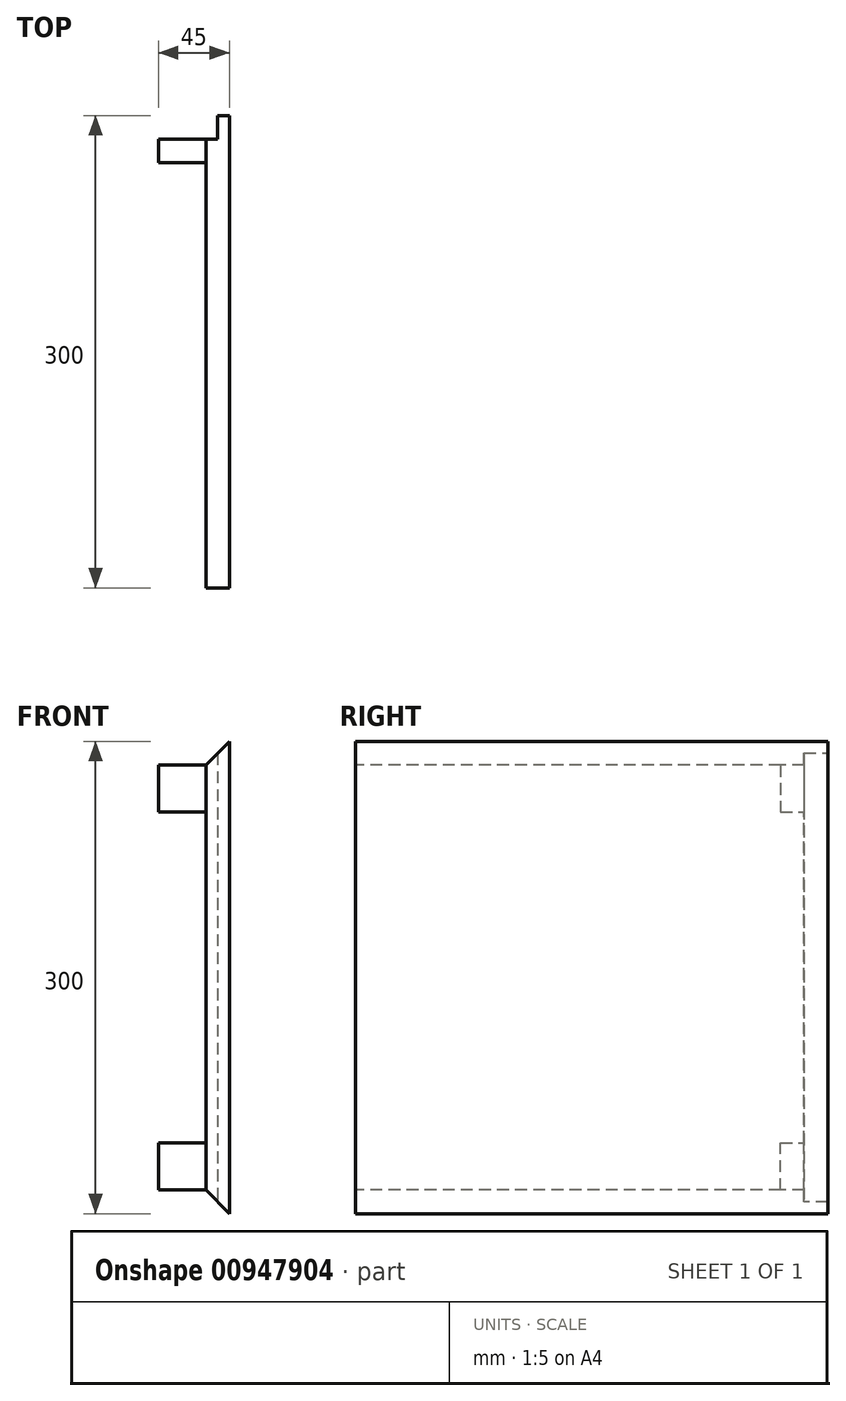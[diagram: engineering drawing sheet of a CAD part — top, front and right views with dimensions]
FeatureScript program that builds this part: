
annotation { "Feature Type Name" : "Feature", "Feature Type Description" : "" }
export const myFeature = defineFeature(function(context is Context, id is Id, definition is map)
    precondition{}
    {
        {
            var Q0;
            Q0=qCreatedBy(makeId("Right.planeOp"),FACE);
            cPlane(context, id + "F0", {"entities" : qUnion([Q0]), "cplaneType" : CPlaneType.OFFSET, "offset" : 100 * mm, "width" : 150 * mm, "height" : 150 * mm});
        }
        {
            var Q0;
            Q0=qCreatedBy(makeId("Front.planeOp"),FACE);
            cPlane(context, id + "F1", {"entities" : qUnion([Q0]), "cplaneType" : CPlaneType.OFFSET, "offset" : 150 * mm, "width" : 150 * mm, "height" : 150 * mm});
        }
        {
            var Q0;
            Q0=qCreatedBy(makeId("Front.planeOp"),FACE);
            cPlane(context, id + "F2", {"entities" : qUnion([Q0]), "cplaneType" : CPlaneType.OFFSET, "offset" : 150 * mm, "oppositeDirection" : true, "width" : 150 * mm, "height" : 150 * mm});
        }
        {
            var Q0;
            Q0=qCreatedBy(makeId("Top.planeOp"),FACE);
            cPlane(context, id + "F3", {"entities" : qUnion([Q0]), "cplaneType" : CPlaneType.OFFSET, "offset" : 300 * mm, "width" : 150 * mm, "height" : 150 * mm});
        }
        {
            var Q0;
            Q0=qCreatedBy(id+"F1.planeOp",FACE);
            var sketch = newSketch(context, id + "F4", { "sketchPlane" : qUnion([Q0])});
            skLineSegment(sketch, "E0", {"start": v(100, 0) * mm, "end": v(100, 300) * mm});
            skLineSegment(sketch, "E1", {"start": v(100, 300) * mm, "end": v(85, 285) * mm});
            skLineSegment(sketch, "E2", {"start": v(85, 285) * mm, "end": v(85, 15) * mm});
            skLineSegment(sketch, "E3", {"start": v(85, 15) * mm, "end": v(100, 0) * mm});
            skSolve(sketch);
        }
        {
            var Q0;
            Q0 = qSketchRegion(id + "F4", true);
            var Q1;
            Q1=qCreatedBy(id+"F2.planeOp",FACE);
            extrude(context, id + "F5", {"entities" : qUnion([Q0]), "endBound" : BoundingType.UP_TO_SURFACE, "oppositeDirection" : true, "depth" : 25 * mm, "endBoundEntityFace" : qUnion([Q1]), "offsetDistance" : 25 * mm});
        }
        {
            var Q0;
            Q0=qCreatedBy(id+"F2.planeOp",FACE);
            var sketch = newSketch(context, id + "F6", { "sketchPlane" : qUnion([Q0])});
            skLineSegment(sketch, "E4.bottom", {"start": v(92.5, 300) * mm, "end": v(80, 300) * mm});
            skLineSegment(sketch, "E4.top", {"start": v(92.5, 0) * mm, "end": v(80, 0) * mm});
            skLineSegment(sketch, "E4.left", {"start": v(92.5, 300) * mm, "end": v(92.5, 0) * mm});
            skLineSegment(sketch, "E4.right", {"start": v(80, 300) * mm, "end": v(80, 0) * mm});
            skSolve(sketch);
        }
        {
            var Q0;
            Q0 = qSketchRegion(id + "F6", true);
            extrude(context, id + "F7", {"entities" : qUnion([Q0]), "operationType" : NewBodyOperationType.REMOVE, "depth" : 15 * mm, "offsetDistance" : 25 * mm});
        }
        {
            var Q0;
            Q0=qCreatedBy(makeId("Front.planeOp"),FACE);
            cPlane(context, id + "F8", {"entities" : qUnion([Q0]), "cplaneType" : CPlaneType.OFFSET, "offset" : (150 - 15) * mm, "oppositeDirection" : true, "width" : 150 * mm, "height" : 150 * mm});
        }
        {
            var Q0;
            Q0=qCreatedBy(id+"F8.planeOp",FACE);
            var sketch = newSketch(context, id + "F9", { "sketchPlane" : qUnion([Q0])});
            skLineSegment(sketch, "E5.bottom", {"start": v(85, 285) * mm, "end": v(55, 285) * mm});
            skLineSegment(sketch, "E5.top", {"start": v(85, 255) * mm, "end": v(55, 255) * mm});
            skLineSegment(sketch, "E5.left", {"start": v(85, 285) * mm, "end": v(85, 255) * mm});
            skLineSegment(sketch, "E5.right", {"start": v(55, 285) * mm, "end": v(55, 255) * mm});
            skLineSegment(sketch, "E6.bottom", {"start": v(85, 15) * mm, "end": v(55, 15) * mm});
            skLineSegment(sketch, "E6.top", {"start": v(85, 45) * mm, "end": v(55, 45) * mm});
            skLineSegment(sketch, "E6.left", {"start": v(85, 15) * mm, "end": v(85, 45) * mm});
            skLineSegment(sketch, "E6.right", {"start": v(55, 15) * mm, "end": v(55, 45) * mm});
            skSolve(sketch);
        }
        {
            var Q0;
            Q0 = qSketchRegion(id + "F9", true);
            extrude(context, id + "F10", {"entities" : qUnion([Q0]), "operationType" : NewBodyOperationType.ADD, "depth" : 15 * mm, "offsetDistance" : 25 * mm});
        }
    });
